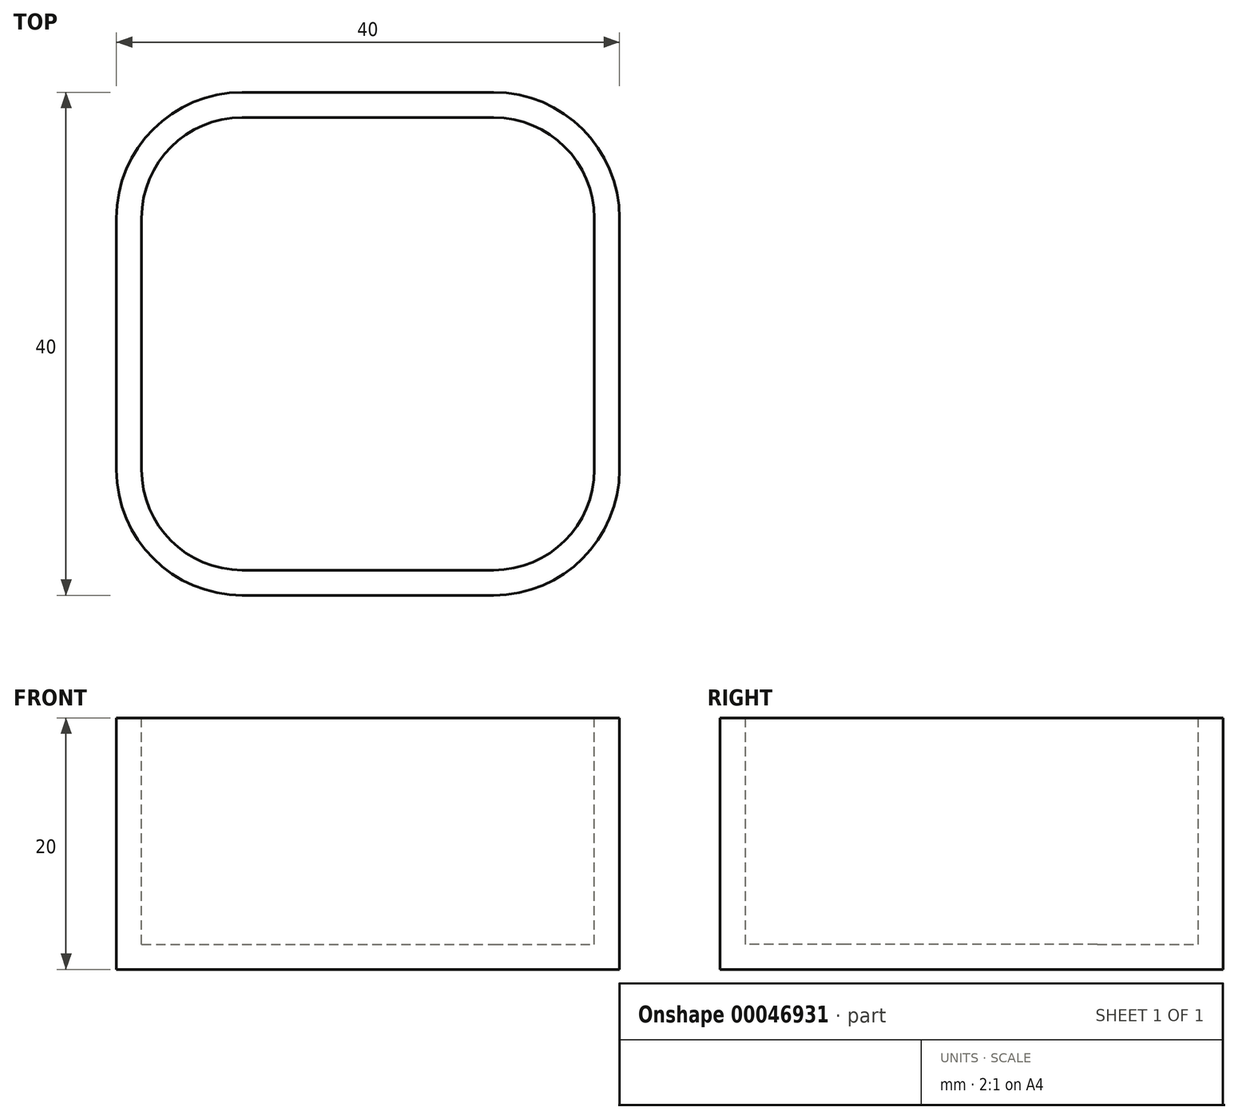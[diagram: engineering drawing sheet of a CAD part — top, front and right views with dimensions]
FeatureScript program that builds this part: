
annotation { "Feature Type Name" : "Feature", "Feature Type Description" : "" }
export const myFeature = defineFeature(function(context is Context, id is Id, definition is map)
    precondition{}
    {
        {
            var Q0;
            Q0=qCreatedBy(makeId("Top.planeOp"),FACE);
            var sketch = newSketch(context, id + "F0", { "sketchPlane" : qUnion([Q0])});
            skLineSegment(sketch, "E0.bottom", {"start": v(-20, 20) * mm, "end": v(20, 20) * mm});
            skLineSegment(sketch, "E0.top", {"start": v(-20, -20) * mm, "end": v(20, -20) * mm});
            skLineSegment(sketch, "E0.left", {"start": v(-20, 20) * mm, "end": v(-20, -20) * mm});
            skLineSegment(sketch, "E0.right", {"start": v(20, 20) * mm, "end": v(20, -20) * mm});
            skPoint(sketch, "E0.middle", {"position": v(0, 0) * mm});
            skSolve(sketch);
        }
        {
            var Q0;
            Q0 = qSketchRegion(id + "F0", true);
            extrude(context, id + "F1", {"entities" : qUnion([Q0]), "oppositeDirection" : true, "depth" : 20 * mm});
        }
        {
            var Q0;
            Q0=makeQuery(id+"F1.opExtrude","SWEPT_EDGE",EDGE,{"disambiguationData":[OSD([sQuery(id+"F0.wireOp",EDGE,"E0.top"),sQuery(id+"F0.wireOp",EDGE,"E0.left")])]});
            var Q1;
            Q1=makeQuery(id+"F1.opExtrude","SWEPT_EDGE",EDGE,{"disambiguationData":[OSD([sQuery(id+"F0.wireOp",EDGE,"E0.top"),sQuery(id+"F0.wireOp",EDGE,"E0.right")])]});
            var Q2;
            Q2=makeQuery(id+"F1.opExtrude","SWEPT_EDGE",EDGE,{"disambiguationData":[OSD([sQuery(id+"F0.wireOp",EDGE,"E0.bottom"),sQuery(id+"F0.wireOp",EDGE,"E0.right")])]});
            var Q3;
            Q3=makeQuery(id+"F1.opExtrude","SWEPT_EDGE",EDGE,{"disambiguationData":[OSD([sQuery(id+"F0.wireOp",EDGE,"E0.bottom"),sQuery(id+"F0.wireOp",EDGE,"E0.left")])]});
            fillet(context, id + "F2", {"entities" : qUnion([Q0, Q1, Q2, Q3]), "radius" : 10 * mm, "tangentPropagation" : true, "allowEdgeOverflow" : false});
        }
        {
            var Q0;
            Q0=makeQuery(id+"F1.opExtrude","CAP_FACE",FACE,{"disambiguationData":[OSD([sQuery(id+"F0.wireOp",EDGE,"E0.bottom"),sQuery(id+"F0.wireOp",EDGE,"E0.top"),sQuery(id+"F0.wireOp",EDGE,"E0.left"),sQuery(id+"F0.wireOp",EDGE,"E0.right")])],"isStart":true});
            shell(context, id + "F3", {"entities" : qUnion([Q0]), "thickness" : 2 * mm});
        }
    });
